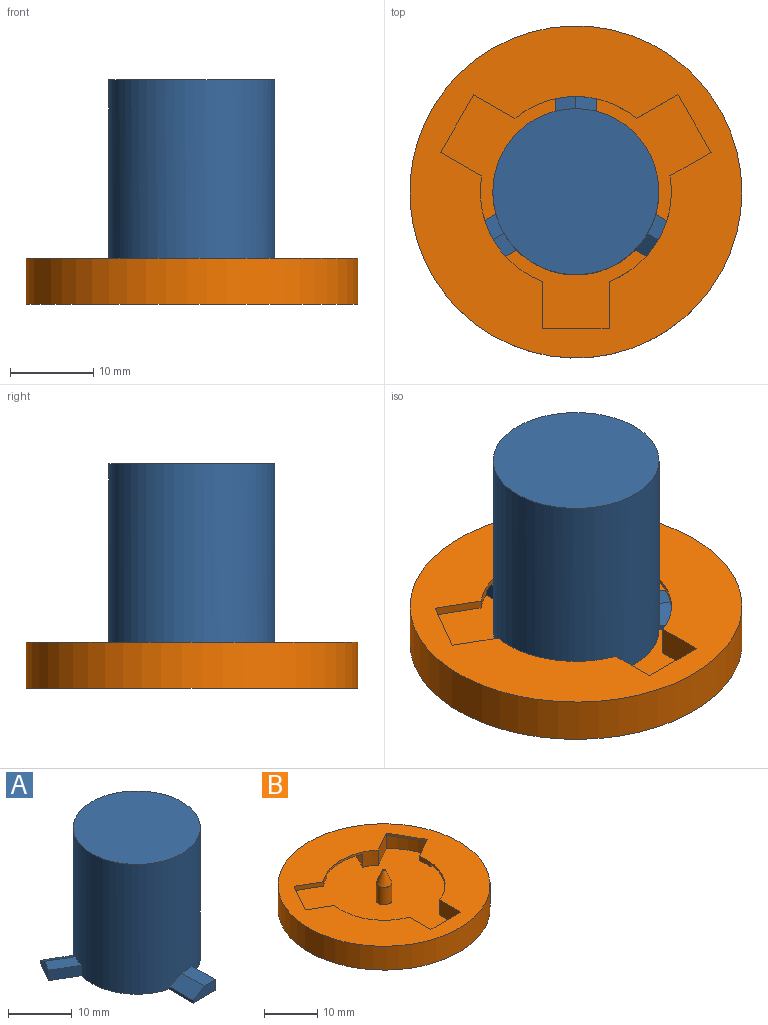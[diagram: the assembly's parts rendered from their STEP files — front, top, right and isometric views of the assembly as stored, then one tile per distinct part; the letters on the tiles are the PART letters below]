
ASSEMBLY  parts=2 mates=1
PART A: 21 faces, bbox 28.5x25x25 mm
  f0: cylinder r=10mm len=25mm, axis (0,0,-1), area 1546.2mm2, adj f1,f2,f3,f4,f5,f6,f8,f9
  f1: plane 20x20mm, normal (0,0,1), area 314.2mm2, adj f0
  f2: plane 28.48x25mm, normal (0,0,-1), area 378.2mm2, adj f0,f3,f4,f7,f8,f9,f12,f13
  f3: plane 5.32x2mm, normal (1,0,0), area 10.6mm2, adj f0,f2,f5,f7
  f4: plane 5.32x0.5mm, normal (-1,0,0), area 2.7mm2, adj f0,f2,f6,f7
  f5: plane 5.32x2.5mm, normal (0,0,1), area 12.8mm2, adj f0,f3,f6,f7
  f6: plane 5.33x2.51mm, normal (-0.51,0,0.86), area 14.9mm2, adj f0,f4,f5,f7
  f7: plane 5x2mm, normal (0,-1,0), area 8.1mm2, adj f2,f3,f4,f5,f6
  f8: plane 4.61x2.66mm, normal (-0.5,0.87,0), area 10.6mm2, adj f0,f2,f10,f12
  f9: plane 4.61x2.66mm, normal (0.5,-0.87,0), area 2.7mm2, adj f0,f2,f11,f12
  f10: plane 5.86x4.67mm, normal (0,0,1), area 12.8mm2, adj f0,f8,f11,f12
  f11: plane 5.59x4.84mm, normal (0.26,-0.45,0.86), area 14.9mm2, adj f0,f9,f10,f12
  f12: plane 4.33x2.5mm, normal (0.87,0.5,0), area 8.1mm2, adj f2,f8,f9,f10,f11
  f13: plane 4.61x2.66mm, normal (-0.5,-0.87,0), area 10.6mm2, adj f0,f2,f15,f17
  f14: plane 4.61x2.66mm, normal (0.5,0.87,0), area 2.7mm2, adj f0,f2,f16,f17
  f15: plane 5.58x4.82mm, normal (0,0,1), area 12.8mm2, adj f0,f13,f16,f17
  f16: plane 5.87x4.68mm, normal (0.26,0.45,0.86), area 14.9mm2, adj f0,f14,f15,f17
  f17: plane 4.33x2.5mm, normal (-0.87,0.5,0), area 8.1mm2, adj f2,f13,f14,f15,f16
  f18: cylinder r=1.5mm len=9.5mm, axis (0,0,-1), area 89.5mm2, adj f19,f20
  f19: plane 3x3mm, normal (0,0,-1), area 7.1mm2, adj f18
  f20: cone r=1.5mm half-angle=45deg, axis (0,0,-1), area 7.8mm2, adj f2,f18
PART B: 37 faces, bbox 40x40x9 mm
  f0: cylinder r=16.98mm len=25.58mm, axis (0,0,-1), area 84.2mm2, adj f1,f2,f8,f17,f19,f29,f30,f33
  f1: plane 33.96x33.88mm, normal (0,0,1), area 821.1mm2, adj f0,f3,f12,f13,f16,f17,f20,f21
  f2: plane 12.81x10.27mm, normal (0,0,-1), area 67.3mm2, adj f0,f20,f29,f33
  f3: cylinder r=16.98mm len=20.91mm, axis (0,0,-1), area 84.2mm2, adj f1,f4,f10,f11,f21,f27,f28,f32
  f4: plane 12.81x10.27mm, normal (0,0,-1), area 67.3mm2, adj f3,f12,f27,f32
  f5: plane 14.21x6.53mm, normal (0,0,-1), area 67.3mm2, adj f16,f24,f25,f31
  f6: cylinder r=20mm len=40mm, axis (0,0,1), area 691.2mm2, adj f7,f23
  f7: plane 40x40mm, normal (0,0,-1), area 1256.6mm2, adj f6
  f8: plane 6.93x4mm, normal (0,0,-1), area 2.6mm2, adj f0,f18
  f9: plane 6.93x4mm, normal (0,0,-1), area 2.6mm2, adj f14,f24
  f10: plane 8x0.48mm, normal (0,0,-1), area 2.6mm2, adj f3,f22
  f11: plane 5.72x1mm, normal (1,0,0), area 5.7mm2, adj f3,f12,f22,f23,f28
  f12: cylinder r=11.5mm len=12.71mm, axis (0,0,-1), area 18.4mm2, adj f1,f4,f11,f13,f23,f27,f28,f32
  f13: plane 4.95x3.5mm, normal (0.5,0.87,0), area 20mm2, adj f1,f12,f14,f23,f24
  f14: plane 6.93x4mm, normal (0.87,-0.5,0), area 4mm2, adj f9,f13,f15,f23
  f15: plane 4.95x2.86mm, normal (-0.5,-0.87,0), area 5.7mm2, adj f14,f16,f23,f24,f26
  f16: cylinder r=11.5mm len=14.68mm, axis (0,0,-1), area 18.4mm2, adj f1,f5,f15,f17,f23,f25,f26,f31
  f17: plane 4.95x3.5mm, normal (0.5,-0.87,0), area 20mm2, adj f0,f1,f16,f18,f23
  f18: plane 6.93x4mm, normal (-0.87,-0.5,0), area 4mm2, adj f8,f17,f19,f23
  f19: plane 4.95x2.86mm, normal (-0.5,0.87,0), area 5.7mm2, adj f0,f18,f20,f23,f30
  f20: cylinder r=11.5mm len=12.71mm, axis (0,0,-1), area 18.4mm2, adj f1,f2,f19,f21,f23,f29,f30,f33
  f21: plane 5.72x3.5mm, normal (-1,0,0), area 20mm2, adj f1,f3,f20,f22,f23
  f22: plane 8x0.5mm, normal (0,1,0), area 4mm2, adj f10,f11,f21,f23
  f23: plane 40x40mm, normal (0,0,1), area 715.5mm2, adj f6,f11,f12,f13,f14,f15,f16,f17
  f24: cylinder r=16.98mm len=23.39mm, axis (0,0,-1), area 84.2mm2, adj f1,f5,f9,f13,f15,f25,f26,f31
  f25: plane 4.98x2.29mm, normal (0.91,0.42,0), area 2.7mm2, adj f5,f16,f24,f26
  f26: plane 7.48x6.57mm, normal (0,0,-1), area 25.8mm2, adj f15,f16,f24,f25
  f27: plane 4.47x3.16mm, normal (-0.82,0.58,0), area 2.7mm2, adj f3,f4,f12,f28
  f28: plane 7.11x5.8mm, normal (0,0,-1), area 25.8mm2, adj f3,f11,f12,f27
  f29: plane 5.46x0.5mm, normal (-0.09,-1,0), area 2.7mm2, adj f0,f2,f20,f30
  f30: plane 6.34x5.64mm, normal (0,0,-1), area 25.8mm2, adj f0,f19,f20,f29
  f31: plane 4.98x3mm, normal (-0.91,0.42,0), area 16.4mm2, adj f1,f5,f16,f24
  f32: plane 5.46x3mm, normal (0.09,-1,0), area 16.4mm2, adj f1,f3,f4,f12
  f33: plane 4.47x3.16mm, normal (0.82,0.58,0), area 16.4mm2, adj f0,f1,f2,f20
  f34: cylinder r=1.5mm len=4mm, axis (0,0,-1), area 37.7mm2, adj f1,f36
  f35: plane 0.5x0.5mm, normal (0,0,1), area 0.2mm2, adj f36
  f36: cone r=1.5mm half-angle=22.6deg, axis (0,0,-1), area 17.9mm2, adj f34,f35
PLACE A rot(axis=(0,0,-1),60deg) t=(-68.9,-39.34,3.05)mm
PLACE B t=(-68.9,-39.34,3.05)mm fixed
MATE revolute A.f18 <-> B.f34  axis (0,0,-1) through (-68.9,-39.34,3.05)mm
